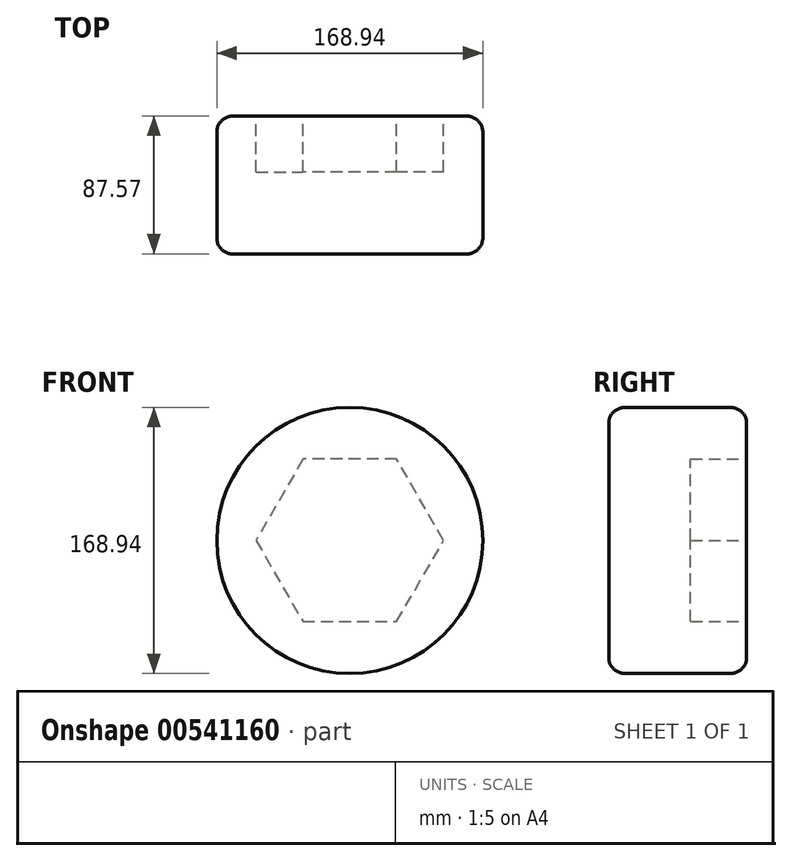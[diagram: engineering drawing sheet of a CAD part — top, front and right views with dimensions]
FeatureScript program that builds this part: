
annotation { "Feature Type Name" : "Feature", "Feature Type Description" : "" }
export const myFeature = defineFeature(function(context is Context, id is Id, definition is map)
    precondition{}
    {
        {
            var Q0;
            Q0=qCreatedBy(makeId("Front.planeOp"),FACE);
            var sketch = newSketch(context, id + "F0", { "sketchPlane" : qUnion([Q0])});
            skCircle(sketch, "E0", {"center": v(0, 0) * mm, "radius": 84.47 * mm});
            skSolve(sketch);
        }
        {
            var Q0;
            Q0 = qSketchRegion(id + "F0", true);
            extrude(context, id + "F1", {"entities" : qUnion([Q0]), "depth" : 87.57 * mm, "offsetDistance" : 25.4 * mm});
        }
        {
            var Q0;
            Q0=makeQuery(id+"F1.opExtrude","CAP_EDGE",EDGE,{"disambiguationData":[OSD([sQuery(id+"F0.wireOp",EDGE,"E0")])],"isStart":false});
            var Q1;
            Q1=makeQuery(id+"F1.opExtrude","CAP_EDGE",EDGE,{"disambiguationData":[OSD([sQuery(id+"F0.wireOp",EDGE,"E0")])],"isStart":true});
            fillet(context, id + "F2", {"entities" : qUnion([Q0, Q1]), "radius" : 10.16 * mm, "tangentPropagation" : true, "allowEdgeOverflow" : false});
        }
        {
            var Q0;
            Q0=makeQuery(id+"F1.opExtrude","CAP_FACE",FACE,{"disambiguationData":[OSD([sQuery(id+"F0.wireOp",EDGE,"E0")])],"isStart":true});
            var sketch = newSketch(context, id + "F3", { "sketchPlane" : qUnion([Q0])});
            skCircle(sketch, "E1.cCircle", {"center": v(0, 0) * mm, "radius": 51.59 * mm, "construction": true});
            skLineSegment(sketch, "E1.0", {"start": v(-29.79, 51.59) * mm, "end": v(29.79, 51.59) * mm});
            skLineSegment(sketch, "E1.1", {"start": v(29.79, 51.59) * mm, "end": v(59.57, 0) * mm});
            skLineSegment(sketch, "E1.2", {"start": v(59.57, 0) * mm, "end": v(29.79, -51.59) * mm});
            skLineSegment(sketch, "E1.3", {"start": v(29.79, -51.59) * mm, "end": v(-29.79, -51.59) * mm});
            skLineSegment(sketch, "E1.4", {"start": v(-29.79, -51.59) * mm, "end": v(-59.57, 0) * mm});
            skLineSegment(sketch, "E1.5", {"start": v(-59.57, 0) * mm, "end": v(-29.79, 51.59) * mm});
            skPoint(sketch, "E1.0.midPoint", {"position": v(0, 51.59) * mm});
            skSolve(sketch);
        }
        {
            var Q0;
            Q0 = qSketchRegion(id + "F3", true);
            extrude(context, id + "F4", {"entities" : qUnion([Q0]), "operationType" : NewBodyOperationType.REMOVE, "oppositeDirection" : true, "depth" : 35.56 * mm, "offsetDistance" : 25.4 * mm});
        }
    });
